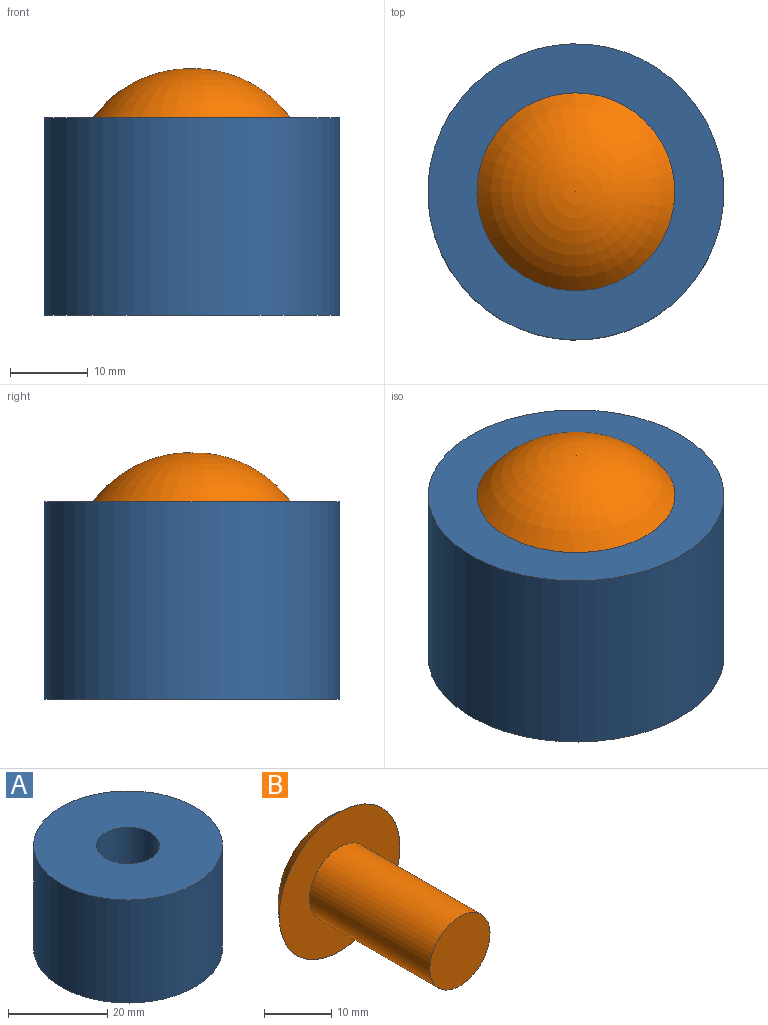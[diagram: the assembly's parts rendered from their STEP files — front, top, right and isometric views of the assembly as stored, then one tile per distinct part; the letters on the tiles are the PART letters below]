
ASSEMBLY  parts=2 mates=1
PART A: 4 faces, bbox 38.1x38.1x25.4 mm
  f0: cylinder r=6.35mm len=25.4mm, axis (0,0,-1), area 1013.4mm2, adj f2,f3
  f1: cylinder r=19.05mm len=38.1mm, axis (0,0,-1), area 3040.2mm2, adj f2,f3
  f2: plane 38.1x38.1mm, normal (0,0,1), area 1013.4mm2, adj f0,f1
  f3: plane 38.1x38.1mm, normal (0,0,-1), area 1013.4mm2, adj f0,f1
PART B: 4 faces, bbox 25.5x32x25.5 mm
  f0: cylinder r=6.35mm len=25.4mm, axis (0,1,0), area 1013.4mm2, adj f1,f2
  f1: plane 12.7x12.7mm, normal (0,-1,0), area 126.7mm2, adj f0
  f2: plane 25.47x25.47mm, normal (0,-1,0), area 382.7mm2, adj f0,f3
  f3: torus R=0.28mm, axis (0,-1,0), area 639.4mm2, adj f2
PLACE A t=(-19.15,-7.22,-6.94)mm
PLACE B rot(axis=(1,0,0),90deg) t=(-19.15,-7.22,18.46)mm
MATE fastened B.f3 <-> A.f1  axis (0,0,-1) through (-19.15,-7.22,18.46)mm
